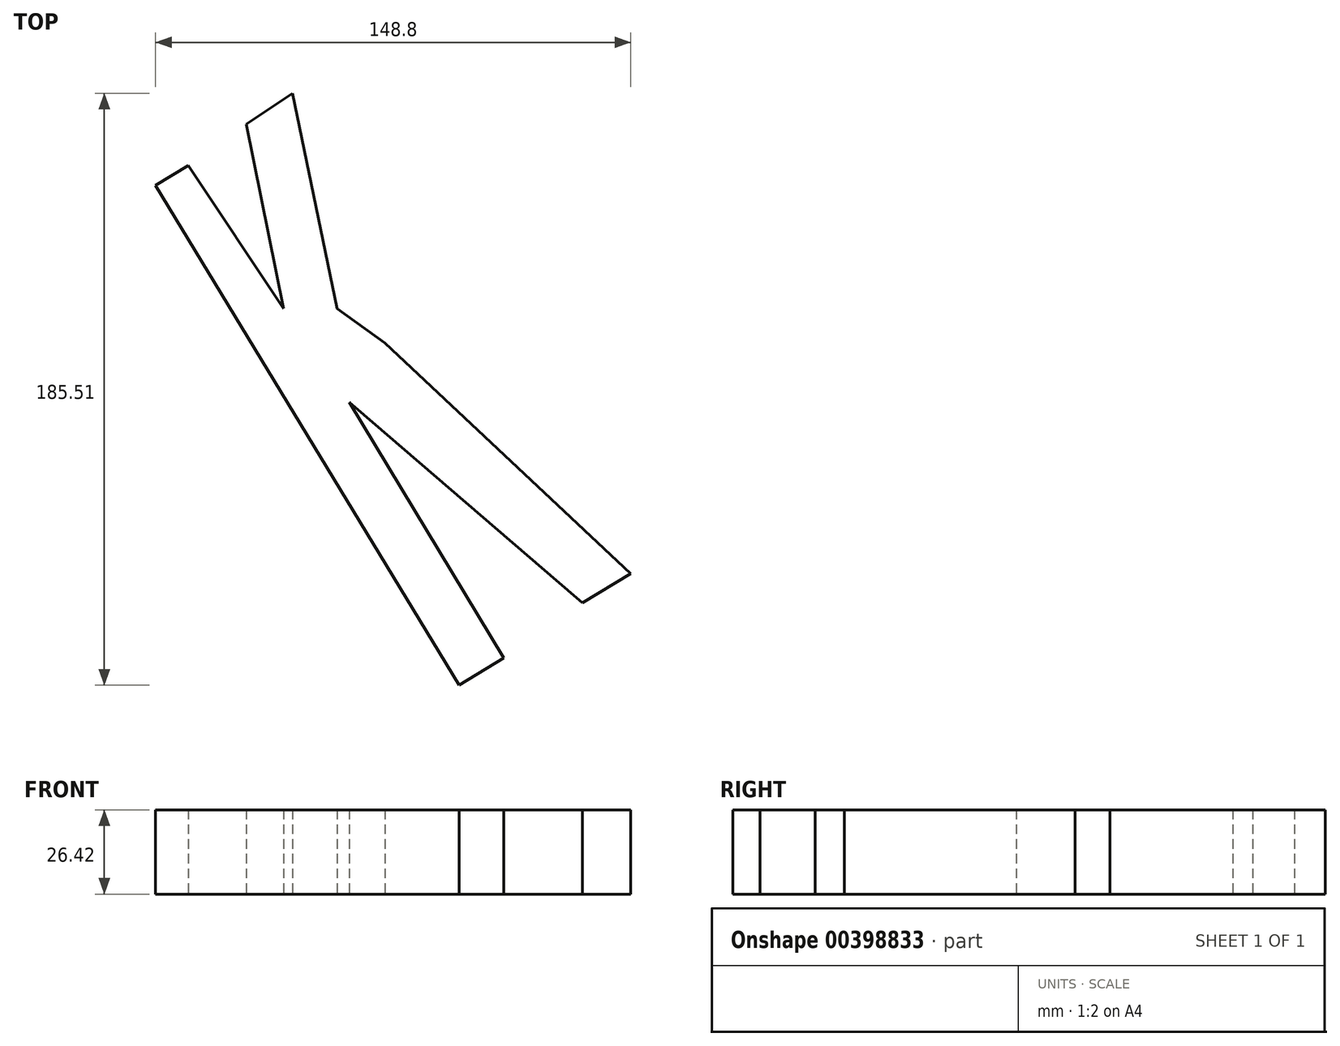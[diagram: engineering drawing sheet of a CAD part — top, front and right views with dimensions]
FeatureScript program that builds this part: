
annotation { "Feature Type Name" : "Feature", "Feature Type Description" : "" }
export const myFeature = defineFeature(function(context is Context, id is Id, definition is map)
    precondition{}
    {
        {
            var Q0;
            Q0=qCreatedBy(makeId("Top.planeOp"),FACE);
            var sketch = newSketch(context, id + "F0", { "sketchPlane" : qUnion([Q0])});
            skLineSegment(sketch, "E0", {"start": v(-82.19, 38.56) * mm, "end": v(12.83, -118.08) * mm});
            skLineSegment(sketch, "E1", {"start": v(12.83, -118.08) * mm, "end": v(26.91, -109.54) * mm});
            skLineSegment(sketch, "E2", {"start": v(-21.49, -29.33) * mm, "end": v(26.91, -109.54) * mm});
            skLineSegment(sketch, "E3", {"start": v(-21.49, -29.33) * mm, "end": v(51.49, -92.23) * mm});
            skLineSegment(sketch, "E4", {"start": v(51.49, -92.23) * mm, "end": v(66.6, -83.11) * mm});
            skLineSegment(sketch, "E5", {"start": v(-10.29, -10.87) * mm, "end": v(66.6, -83.11) * mm});
            skLineSegment(sketch, "E6", {"start": v(-82.19, 38.56) * mm, "end": v(-71.97, 44.75) * mm});
            skLineSegment(sketch, "E7", {"start": v(-71.97, 44.75) * mm, "end": v(-42.1, 0) * mm});
            skLineSegment(sketch, "E8", {"start": v(-42.1, 0) * mm, "end": v(-53.8, 57.77) * mm});
            skLineSegment(sketch, "E9", {"start": v(-53.8, 57.77) * mm, "end": v(-39.32, 67.43) * mm});
            skLineSegment(sketch, "E10", {"start": v(-39.32, 67.43) * mm, "end": v(-25.36, 0) * mm});
            skLineSegment(sketch, "E11", {"start": v(-25.36, 0) * mm, "end": v(-10.29, -10.87) * mm});
            skSolve(sketch);
        }
        {
            var Q0;
            Q0 = qSketchRegion(id + "F0", true);
            extrude(context, id + "F1", {"entities" : qUnion([Q0]), "depth" : 26.42 * mm});
        }
    });
